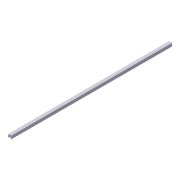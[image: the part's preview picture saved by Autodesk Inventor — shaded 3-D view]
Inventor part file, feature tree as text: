
AUTODESK INVENTOR PART (.ipt)
format: ipt  version: 2012 (Build 160160000, 160)  size: 67,072 bytes
history: native  units: in
note: dims shown in document units (in); Inventor stores cm internally (conversion verified against a paired STEP export)
features: extrude x1, sketch x1
ambient origin geometry x8: Origin, YZ Plane, XZ Plane, XY Plane, X Axis, Y Axis, Z Axis, Center Point
bodies: Solid1 (feature_tree)
feature tree (2):
  extrude  "Extrusion1"  Depth=0.75in
  sketch  "Sketch1"  dims[d0=0.75in d1=0.75in d2=0.125in d3=0.125in d4=39.0in d5=0.0in]
